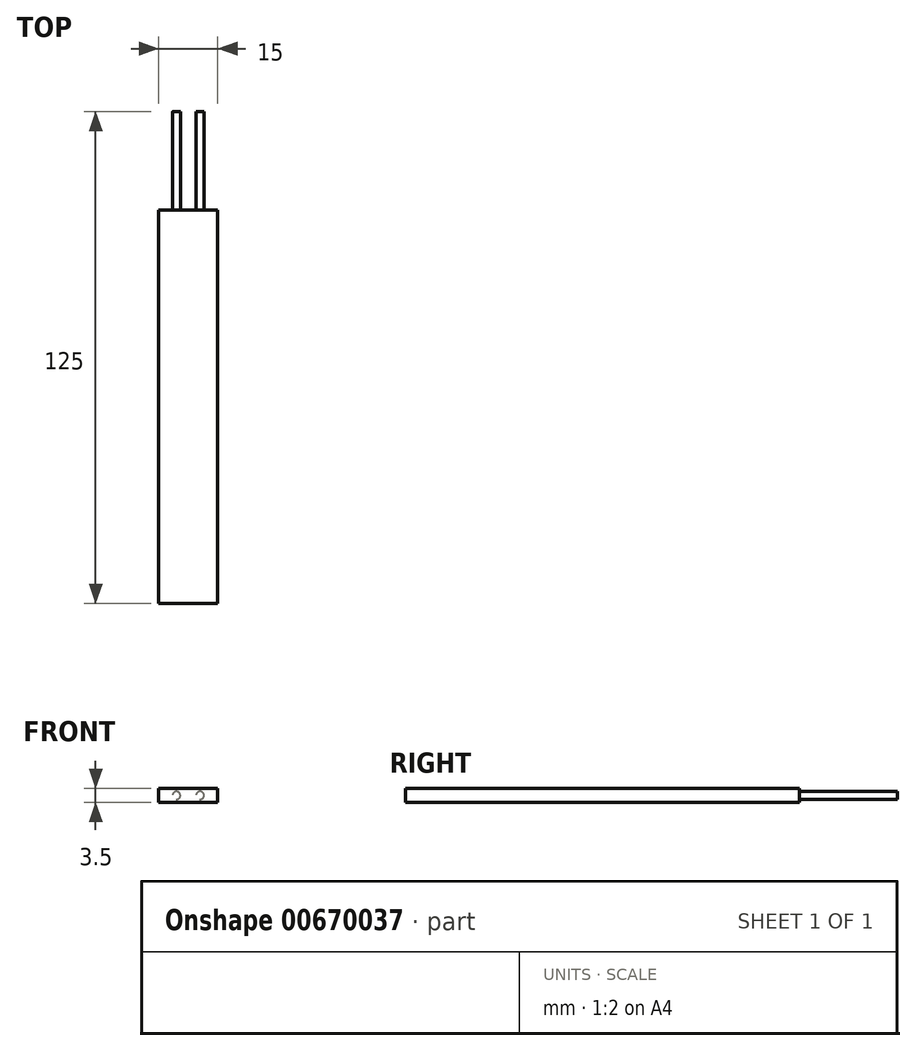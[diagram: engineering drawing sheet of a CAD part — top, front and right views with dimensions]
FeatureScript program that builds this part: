
annotation { "Feature Type Name" : "Feature", "Feature Type Description" : "" }
export const myFeature = defineFeature(function(context is Context, id is Id, definition is map)
    precondition{}
    {
        {
            var Q0;
            Q0=qCreatedBy(makeId("Top.planeOp"),FACE);
            var sketch = newSketch(context, id + "F0", { "sketchPlane" : qUnion([Q0])});
            skLineSegment(sketch, "E0.bottom", {"start": v(-7.5, 50) * mm, "end": v(7.5, 50) * mm});
            skLineSegment(sketch, "E0.top", {"start": v(-7.5, -50) * mm, "end": v(7.5, -50) * mm});
            skLineSegment(sketch, "E0.left", {"start": v(-7.5, 50) * mm, "end": v(-7.5, -50) * mm});
            skLineSegment(sketch, "E0.right", {"start": v(7.5, 50) * mm, "end": v(7.5, -50) * mm});
            skPoint(sketch, "E0.middle", {"position": v(0, 0) * mm});
            skSolve(sketch);
        }
        {
            var Q0;
            Q0 = qSketchRegion(id + "F0", true);
            extrude(context, id + "F1", {"entities" : qUnion([Q0]), "endBound" : BoundingType.SYMMETRIC, "depth" : 3.5 * mm, "offsetDistance" : 25 * mm});
        }
        {
            var Q0;
            Q0=makeQuery(id+"F1.opExtrude","SWEPT_FACE",FACE,{"disambiguationData":[OSD([sQuery(id+"F0.wireOp",EDGE,"E0.bottom")])]});
            var sketch = newSketch(context, id + "F2", { "sketchPlane" : qUnion([Q0])});
            skCircle(sketch, "E1", {"center": v(3, 0) * mm, "radius": 1 * mm});
            skCircle(sketch, "E2", {"center": v(-3, 0) * mm, "radius": 1 * mm});
            skSolve(sketch);
        }
        {
            var Q0;
            Q0 = qSketchRegion(id + "F2", true);
            extrude(context, id + "F3", {"entities" : qUnion([Q0]), "operationType" : NewBodyOperationType.ADD, "depth" : 25 * mm, "offsetDistance" : 25 * mm});
        }
    });
